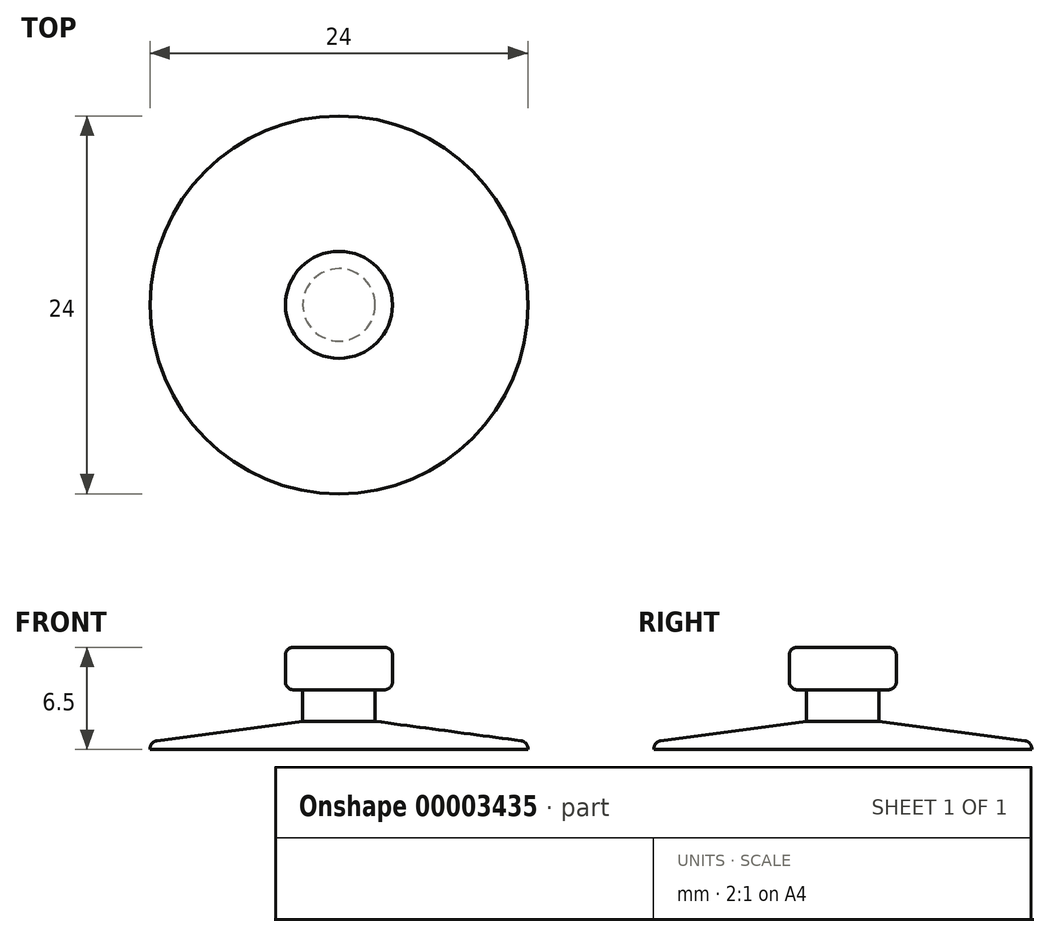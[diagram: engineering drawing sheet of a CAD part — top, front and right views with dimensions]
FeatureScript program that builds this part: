
annotation { "Feature Type Name" : "Feature", "Feature Type Description" : "" }
export const myFeature = defineFeature(function(context is Context, id is Id, definition is map)
    precondition{}
    {
        {
            var Q0;
            Q0=qCreatedBy(makeId("Front.planeOp"),FACE);
            var sketch = newSketch(context, id + "F0", { "sketchPlane" : qUnion([Q0])});
            skLineSegment(sketch, "E0", {"start": v(0, 0) * mm, "end": v(-12, 0) * mm});
            skLineSegment(sketch, "E1", {"start": v(-12, 0) * mm, "end": v(-12, 0.06) * mm});
            skLineSegment(sketch, "E2", {"start": v(-11.57, 0.56) * mm, "end": v(-2.3, 1.8) * mm});
            skLineSegment(sketch, "E3", {"start": v(-2.3, 1.8) * mm, "end": v(-2.3, 3.8) * mm});
            skLineSegment(sketch, "E4", {"start": v(-2.3, 3.8) * mm, "end": v(-2.9, 3.8) * mm});
            skLineSegment(sketch, "E5", {"start": v(-3.4, 4.3) * mm, "end": v(-3.4, 6) * mm});
            skLineSegment(sketch, "E6", {"start": v(-2.9, 6.5) * mm, "end": v(0, 6.5) * mm});
            skLineSegment(sketch, "E7", {"start": v(0, 6.5) * mm, "end": v(0, 0) * mm});
            skPoint(sketch, "E8.visualSharp", {"position": v(-3.4, 6.5) * mm});
            skArc(sketch, "E8.filletArc", {"start": v(-2.9, 6.5) * mm, "mid": v(-3.25, 6.35) * mm, "end": v(-3.4, 6) * mm});
            skPoint(sketch, "E9.visualSharp", {"position": v(-3.4, 3.8) * mm});
            skArc(sketch, "E9.filletArc", {"start": v(-3.4, 4.3) * mm, "mid": v(-3.25, 3.95) * mm, "end": v(-2.9, 3.8) * mm});
            skPoint(sketch, "E10.visualSharp", {"position": v(-12, 0.5) * mm});
            skArc(sketch, "E10.filletArc", {"start": v(-11.57, 0.56) * mm, "mid": v(-11.88, 0.4) * mm, "end": v(-12, 0.06) * mm});
            skSolve(sketch);
        }
        {
            var Q0;
            Q0=makeQuery(id+"F0.imprint","IMPRINT",FACE,{"disambiguationData":[TD([[makeQuery(id+"F0.imprint","IMPRINT",EDGE,{"derivedFrom":sQuery(id+"F0.wireOp",EDGE,"E0")}),-1.0]])]});
            var Q1;
            Q1=sQuery(id+"F0.wireOp",EDGE,"E7");
            revolve(context, id + "F1", {"entities" : qUnion([Q0]), "axis" : qUnion([Q1]), "revolveType" : RevolveType.FULL});
        }
    });
